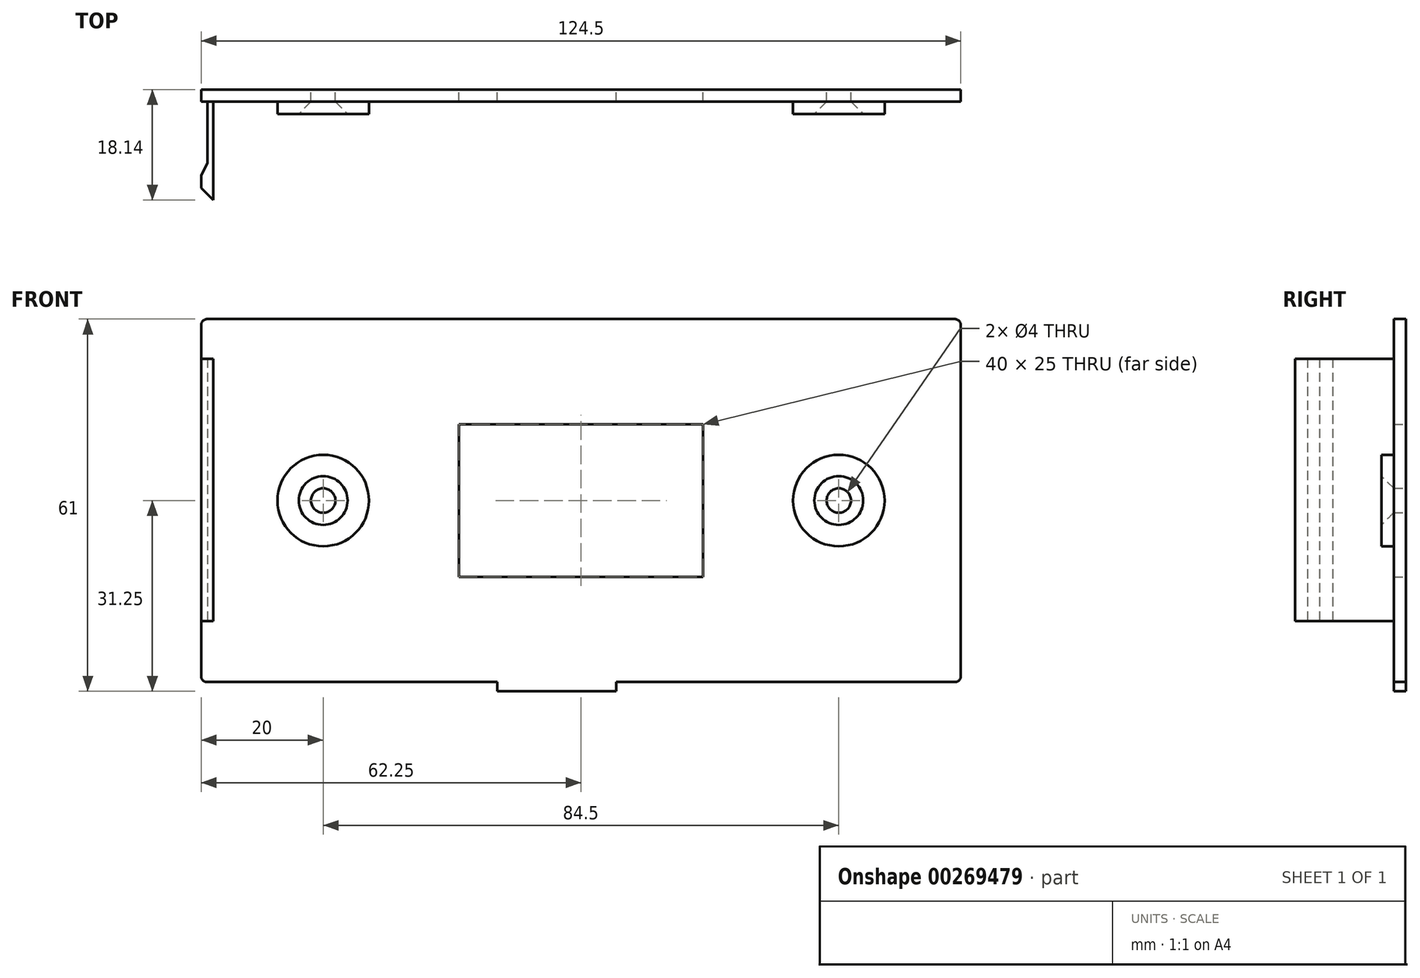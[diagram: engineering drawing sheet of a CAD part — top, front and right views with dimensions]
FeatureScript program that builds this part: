
annotation { "Feature Type Name" : "Feature", "Feature Type Description" : "" }
export const myFeature = defineFeature(function(context is Context, id is Id, definition is map)
    precondition{}
    {
        {
            var Q0;
            Q0=qCreatedBy(makeId("Front.planeOp"),FACE);
            var sketch = newSketch(context, id + "F0", { "sketchPlane" : qUnion([Q0])});
            skLineSegment(sketch, "E0.bottom", {"start": v(-62.25, 29.75) * mm, "end": v(62.25, 29.75) * mm});
            skLineSegment(sketch, "E0.top", {"start": v(-62.25, -29.75) * mm, "end": v(-13.75, -29.75) * mm});
            skLineSegment(sketch, "E0.left", {"start": v(-62.25, 29.75) * mm, "end": v(-62.25, -29.75) * mm});
            skLineSegment(sketch, "E0.right", {"start": v(62.25, 29.75) * mm, "end": v(62.25, -29.75) * mm});
            skPoint(sketch, "E0.middle", {"position": v(0, 0) * mm});
            skCircle(sketch, "E1", {"center": v(-42.25, 0) * mm, "radius": 2 * mm});
            skCircle(sketch, "E2", {"center": v(42.25, 0) * mm, "radius": 2 * mm});
            skLineSegment(sketch, "E3.bottom", {"start": v(-20, 12.5) * mm, "end": v(20, 12.5) * mm});
            skLineSegment(sketch, "E3.top", {"start": v(-20, -12.5) * mm, "end": v(20, -12.5) * mm});
            skLineSegment(sketch, "E3.left", {"start": v(-20, 12.5) * mm, "end": v(-20, -12.5) * mm});
            skLineSegment(sketch, "E3.right", {"start": v(20, 12.5) * mm, "end": v(20, -12.5) * mm});
            skLineSegment(sketch, "E4", {"start": v(-13.75, -29.75) * mm, "end": v(-13.75, -31.25) * mm});
            skLineSegment(sketch, "E5", {"start": v(-13.75, -31.25) * mm, "end": v(5.75, -31.25) * mm});
            skLineSegment(sketch, "E6", {"start": v(5.75, -31.25) * mm, "end": v(5.75, -29.75) * mm});
            skLineSegment(sketch, "E7.trimOffspring", {"start": v(5.75, -29.75) * mm, "end": v(62.25, -29.75) * mm});
            skSolve(sketch);
        }
        {
            var Q0;
            Q0=makeQuery(id+"F0.imprint","IMPRINT",FACE,{"disambiguationData":[TD([[makeQuery(id+"F0.imprint","IMPRINT",EDGE,{"derivedFrom":sQuery(id+"F0.wireOp",EDGE,"E0.bottom")}),-1.0]])]});
            extrude(context, id + "F1", {"entities" : qUnion([Q0]), "depth" : 2 * mm});
        }
        {
            var Q0;
            Q0=makeQuery(id+"F1.opExtrude","SWEPT_FACE",FACE,{"disambiguationData":[OSD([sQuery(id+"F0.wireOp",EDGE,"E0.top")])]});
            var sketch = newSketch(context, id + "F2", { "sketchPlane" : qUnion([Q0])});
            skLineSegment(sketch, "E8", {"start": v(-61.25, 2) * mm, "end": v(-61.25, 12) * mm});
            skLineSegment(sketch, "E9", {"start": v(-61.25, 12) * mm, "end": v(-62.25, 14.14) * mm});
            skLineSegment(sketch, "E10", {"start": v(-60.25, 18.14) * mm, "end": v(-60.25, 2) * mm});
            skLineSegment(sketch, "E11", {"start": v(-62.25, 14.14) * mm, "end": v(-62.25, 16.14) * mm});
            skLineSegment(sketch, "E12", {"start": v(-62.25, 16.14) * mm, "end": v(-60.25, 18.14) * mm});
            skLineSegment(sketch, "E13.MirrorCS", {"start": v(61.25, 12) * mm, "end": v(62.25, 14.14) * mm});
            skLineSegment(sketch, "E14.MirrorCS", {"start": v(62.25, 14.14) * mm, "end": v(62.25, 16.14) * mm});
            skLineSegment(sketch, "E15.MirrorCS", {"start": v(62.25, 16.14) * mm, "end": v(60.25, 18.14) * mm});
            skLineSegment(sketch, "E16.MirrorCS", {"start": v(60.25, 18.14) * mm, "end": v(60.25, 2) * mm});
            skLineSegment(sketch, "E17.MirrorCS", {"start": v(61.25, 2) * mm, "end": v(61.25, 12) * mm});
            skLineSegment(sketch, "E18", {"start": v(60.25, 2) * mm, "end": v(61.25, 2) * mm});
            skSolve(sketch);
        }
        {
            var Q0;
            {var subQ1=sQuery(id+"F2.wireOp",EDGE,"E8");Q0=makeQuery(id+"F2.imprint","IMPRINT",FACE,{"disambiguationData":[TD([[makeQuery(id+"F2.imprint","IMPRINT",EDGE,{"derivedFrom":subQ1}),-1.0]])]});}
            var Q1;
            Q1=makeQuery(id+"F2.imprint","IMPRINT",FACE,{"disambiguationData":[TD([[makeQuery(id+"F2.imprint","IMPRINT",EDGE,{"derivedFrom":sQuery(id+"F2.wireOp",EDGE,"E13.MirrorCS")}),1.0]])]});
            extrude(context, id + "F3", {"entities" : qUnion([Q0, Q1]), "operationType" : NewBodyOperationType.ADD, "oppositeDirection" : true, "depth" : 53 * mm, "hasSecondDirection" : true, "secondDirectionOppositeDirection" : true, "secondDirectionDepth" : 10 * mm});
        }
        {
            var Q0;
            Q0=makeQuery(id+"F1.opExtrude","SWEPT_EDGE",EDGE,{"disambiguationData":[OSD([sQuery(id+"F0.wireOp",EDGE,"E0.top"),sQuery(id+"F0.wireOp",EDGE,"E0.left")])]});
            var Q1;
            Q1=makeQuery(id+"F1.opExtrude","SWEPT_EDGE",EDGE,{"disambiguationData":[OSD([sQuery(id+"F0.wireOp",EDGE,"E0.right"),sQuery(id+"F0.wireOp",EDGE,"E7.trimOffspring")])]});
            var Q2;
            Q2=makeQuery(id+"F1.opExtrude","SWEPT_EDGE",EDGE,{"disambiguationData":[OSD([sQuery(id+"F0.wireOp",EDGE,"E0.bottom"),sQuery(id+"F0.wireOp",EDGE,"E0.right")])]});
            var Q3;
            Q3=makeQuery(id+"F1.opExtrude","SWEPT_EDGE",EDGE,{"disambiguationData":[OSD([sQuery(id+"F0.wireOp",EDGE,"E0.bottom"),sQuery(id+"F0.wireOp",EDGE,"E0.left")])]});
            fillet(context, id + "F4", {"entities" : qUnion([Q0, Q1, Q2, Q3]), "radius" : 1 * mm, "tangentPropagation" : true, "allowEdgeOverflow" : false});
        }
        {
            var Q0;
            Q0=makeQuery(id+"F1.opExtrude","CAP_FACE",FACE,{"disambiguationData":[OSD([sQuery(id+"F0.wireOp",EDGE,"E0.bottom"),sQuery(id+"F0.wireOp",EDGE,"E0.top"),sQuery(id+"F0.wireOp",EDGE,"E0.left"),sQuery(id+"F0.wireOp",EDGE,"E0.right"),sQuery(id+"F0.wireOp",EDGE,"E1"),sQuery(id+"F0.wireOp",EDGE,"E2"),sQuery(id+"F0.wireOp",EDGE,"E3.bottom"),sQuery(id+"F0.wireOp",EDGE,"E3.top"),sQuery(id+"F0.wireOp",EDGE,"E3.left"),sQuery(id+"F0.wireOp",EDGE,"E3.right"),sQuery(id+"F0.wireOp",EDGE,"E4"),sQuery(id+"F0.wireOp",EDGE,"E5"),sQuery(id+"F0.wireOp",EDGE,"E6"),sQuery(id+"F0.wireOp",EDGE,"E7.trimOffspring")])],"isStart":false});
            var sketch = newSketch(context, id + "F5", { "sketchPlane" : qUnion([Q0])});
            skCircle(sketch, "E19", {"center": v(-42.25, 0) * mm, "radius": 7.5 * mm});
            skCircle(sketch, "E20", {"center": v(42.25, 0) * mm, "radius": 7.5 * mm});
            skSolve(sketch);
        }
        {
            var Q0;
            Q0=makeQuery(id+"F5.imprint","IMPRINT",FACE,{"disambiguationData":[TD([[makeQuery(id+"F5.imprint","IMPRINT",EDGE,{"derivedFrom":sQuery(id+"F5.wireOp",EDGE,"E19")}),1.0]])]});
            var Q1;
            Q1=makeQuery(id+"F5.imprint","IMPRINT",FACE,{"disambiguationData":[TD([[makeQuery(id+"F5.imprint","IMPRINT",EDGE,{"derivedFrom":sQuery(id+"F5.wireOp",EDGE,"E20")}),1.0]])]});
            extrude(context, id + "F6", {"entities" : qUnion([Q0, Q1]), "operationType" : NewBodyOperationType.ADD, "depth" : 2 * mm});
        }
        {
            var Q0;
            Q0=makeQuery(id+"F6.opExtrude","CAP_EDGE",EDGE,{"disambiguationData":[OSD([sQuery(id+"F0.wireOp",EDGE,"E1")])],"isStart":false});
            var Q1;
            Q1=makeQuery(id+"F6.opExtrude","CAP_EDGE",EDGE,{"disambiguationData":[OSD([sQuery(id+"F0.wireOp",EDGE,"E2")])],"isStart":false});
            chamfer(context, id + "F7", {"entities" : qUnion([Q0, Q1]), "width" : 2 * mm, "tangentPropagation" : true});
        }
    });
